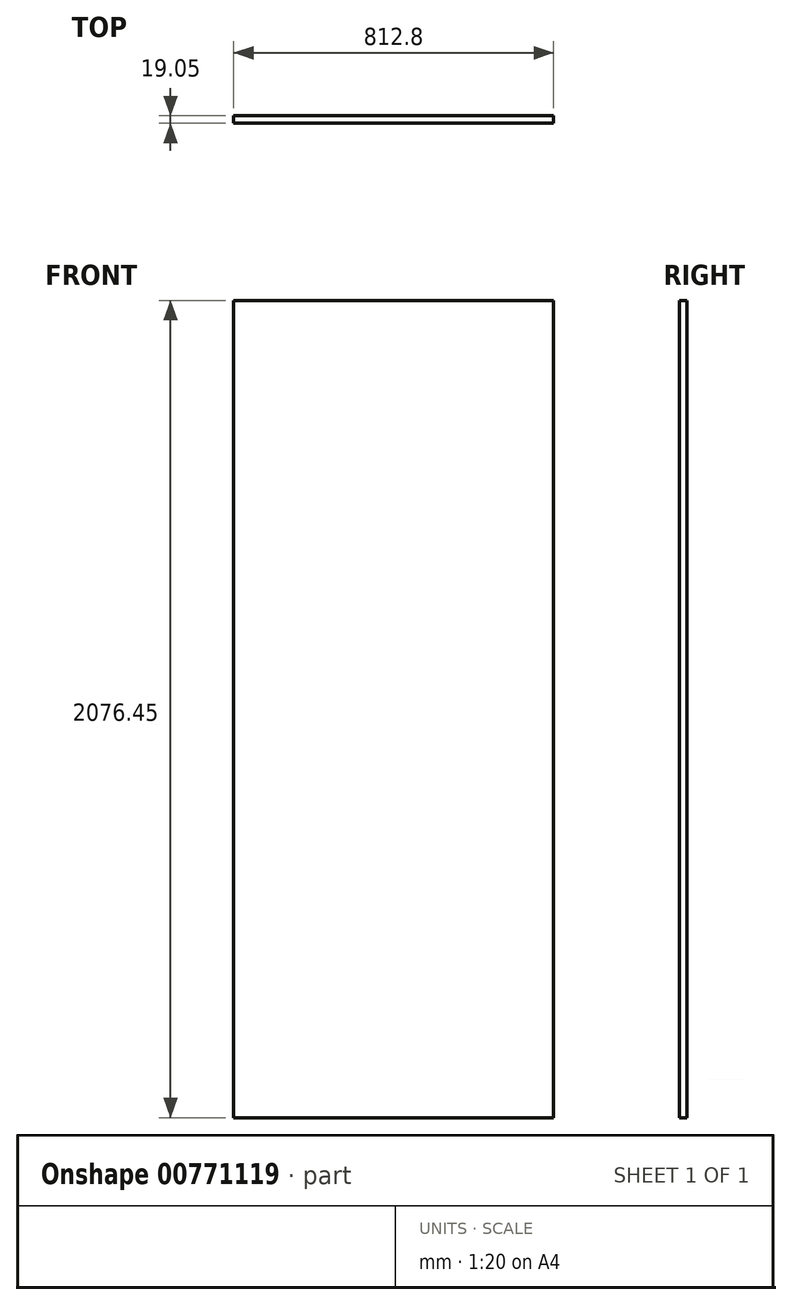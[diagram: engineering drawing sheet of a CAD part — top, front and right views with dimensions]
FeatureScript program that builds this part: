
annotation { "Feature Type Name" : "Feature", "Feature Type Description" : "" }
export const myFeature = defineFeature(function(context is Context, id is Id, definition is map)
    precondition{}
    {
        {
            var Q0;
            Q0=qCreatedBy(makeId("Front.planeOp"),FACE);
            var sketch = newSketch(context, id + "F0", { "sketchPlane" : qUnion([Q0])});
            skLineSegment(sketch, "E0.bottom", {"start": v(0, 0) * mm, "end": v(-812.8, 0) * mm});
            skLineSegment(sketch, "E0.top", {"start": v(0, 2076.45) * mm, "end": v(-812.8, 2076.45) * mm});
            skLineSegment(sketch, "E0.left", {"start": v(0, 0) * mm, "end": v(0, 2076.45) * mm});
            skLineSegment(sketch, "E0.right", {"start": v(-812.8, 0) * mm, "end": v(-812.8, 2076.45) * mm});
            skSolve(sketch);
        }
        {
            var Q0;
            Q0 = qSketchRegion(id + "F0", true);
            extrude(context, id + "F1", {"entities" : qUnion([Q0]), "depth" : 19.05 * mm, "offsetDistance" : 25.4 * mm});
        }
    });
